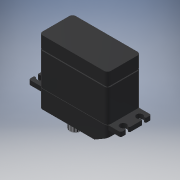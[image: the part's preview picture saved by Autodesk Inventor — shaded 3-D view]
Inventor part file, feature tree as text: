
AUTODESK INVENTOR PART (.ipt)
format: ipt  version: 2019 (Build 230136000, 136)  size: 472,576 bytes
history: native  units: mm
features: fillet x11, extrude x8, sketch x7, projected_geometry x4, plane x2, chamfer x1, mirror x1, sweep x1, pattern_circular x1
ambient origin geometry x8: Origin, YZ Plane, XZ Plane, XY Plane, X Axis, Y Axis, Z Axis, Center Point
bodies: Solid1 (feature_tree)
feature tree (36):
  extrude  "Extrusion1"  Depth=39.5mm
  chamfer  "Chamfer1"  Distance=20.5mm
  plane  "Work Plane1"
  sketch  "Sketch3"  dims[d5=8.0mm d6=2.0mm d7=30.0deg d26=-11.0mm]
  fillet  "Fillet2"  [1 undecoded]
  extrude  "Extrusion3"  Depth=0.65mm
  fillet  "Fillet3"  Radius=2.0mm
  fillet  "Fillet4"  Radius=7.3mm
  mirror  "Mirror1"
  plane  "Work Plane2"
  sweep  "Sweep1"
  sketch  "Sketch7"  dims[d38=2.7mm d39=0.0mm d40=1.0mm]
  extrude  "Extrusion4"  Depth=4.0mm
  extrude  "Extrusion5"  Depth=1.0mm
  extrude  "Extrusion6"  [1 undecoded]
  fillet  "Fillet5"  Radius=0.65mm
  fillet  "Fillet6"  Radius=0.65mm
  fillet  "Fillet7"  Radius=0.65mm
  fillet  "Fillet8"  [1 undecoded]
  fillet  "Fillet9"  Radius=30.0mm
  fillet  "Fillet10"  Radius=13.0mm
  fillet  "Fillet11"  Radius=7.0mm
  extrude  "Extrusion7"  Depth=0.5mm TaperAngle=0.0deg
  sketch  "Sketch8"  dims[d41=0.5mm d42=-8.0mm d43=0.65mm d44=0.65mm d45=0.65mm d46=0.65mm d47=0.0mm d48=30.0mm d49=13.0mm d50=7.0mm d51=2.45mm d52=0.0mm d53=10.0mm d54=0.0mm d55=10.0mm d56=4.0mm d57=4.0mm d58=2.5mm d59=2.0mm d60=0.0mm d61=0.5mm d62=0.5mm d63=0.5mm d64=0.5mm d65=0.5mm d66=0.5mm d67=0.5mm d68=0.3mm d69=0.0mm d70=0.5mm d71=0.5mm d72=5.0mm d73=0.0mm d74=150.0mm d75=360.0deg d77=1.5mm d78=5.0mm d79=0.0mm d80=0.5mm d81=0.0mm]
  extrude  "Extrusion8"  Depth=10.0mm TaperAngle=0.0deg
  pattern_circular  "Circular Pattern1"  [2 undecoded]
  extrude  "Extrusion9"  Depth=0.5mm
  fillet  "Fillet12"  Radius=4.0mm
  sketch  "Sketch1"  dims[d0=42.0mm d2=39.5mm d3=20.5mm d4=0.0mm]
  projected_geometry  "Projected Loop2"
  sketch  "Sketch4"  dims[d27=0.65mm d28=0.65mm d30=2.0mm d31=7.3mm]
  sketch  "Sketch5"  dims[d32=18.75mm d33=10.0mm]
  sketch  "Sketch6"  dims[d34=2.8mm d35=4.0mm]
  projected_geometry  "Projected Loop3"
  projected_geometry  "Projected Loop4"
  projected_geometry  "Projected Loop5"
note: 5 required parameter values undecoded (feature->parameter linkage not recoverable at this tier; creation-order binding heuristic only, values carry confidence <= 0.55)
